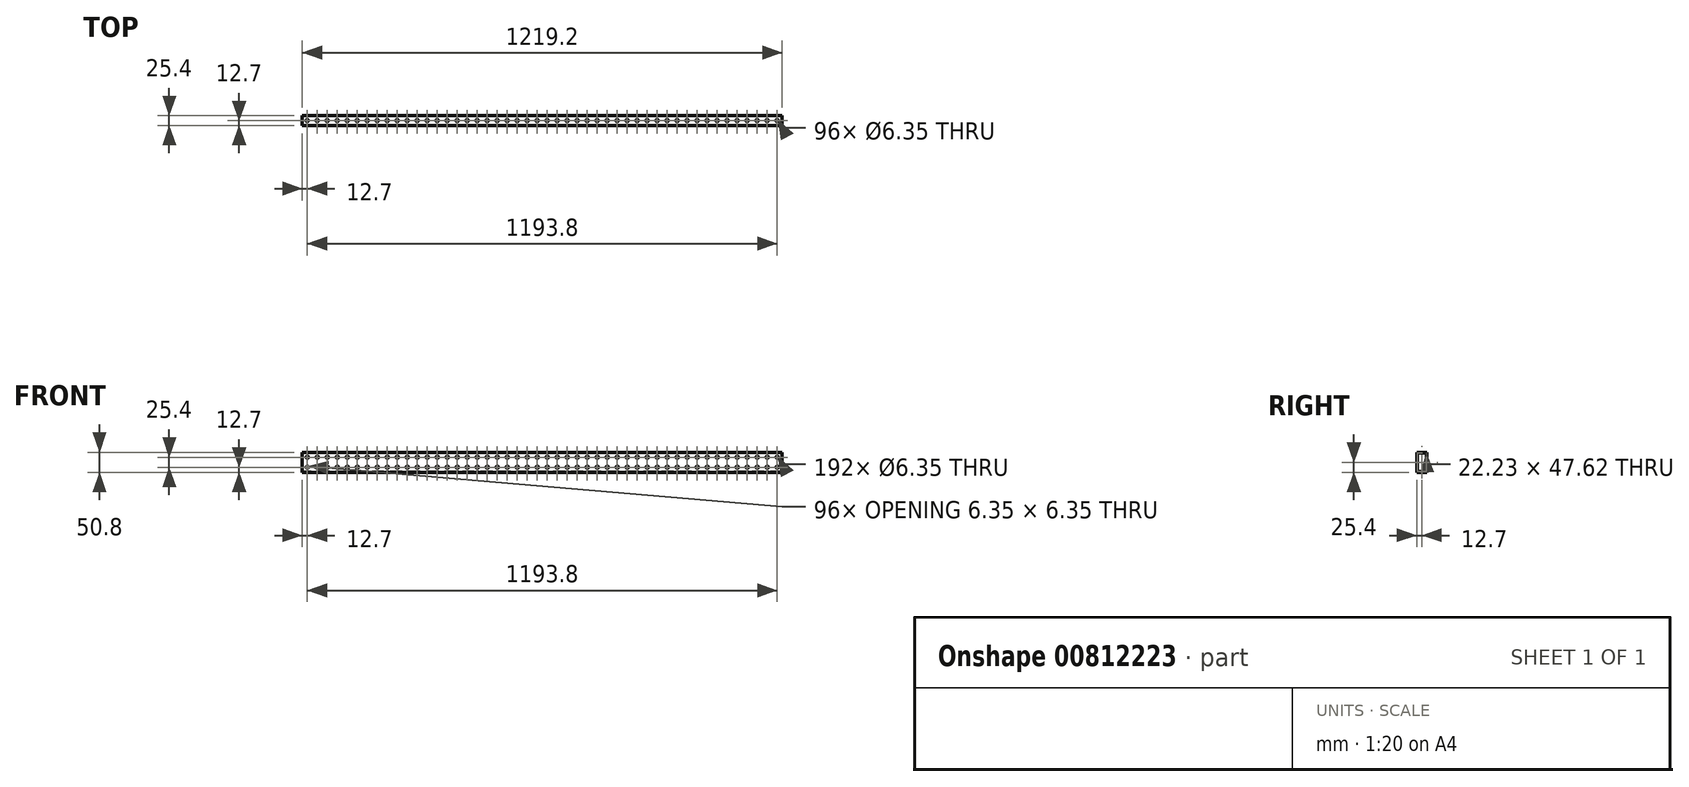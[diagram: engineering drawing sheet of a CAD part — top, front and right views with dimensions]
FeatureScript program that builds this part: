
annotation { "Feature Type Name" : "Feature", "Feature Type Description" : "" }
export const myFeature = defineFeature(function(context is Context, id is Id, definition is map)
    precondition{}
    {
        {
            var Q0;
            Q0=qCreatedBy(makeId("Right.planeOp"),FACE);
            var sketch = newSketch(context, id + "F0", { "sketchPlane" : qUnion([Q0])});
            skLineSegment(sketch, "E0.bottom", {"start": v(-12.7, 25.4) * mm, "end": v(12.7, 25.4) * mm});
            skLineSegment(sketch, "E0.top", {"start": v(-12.7, -25.4) * mm, "end": v(12.7, -25.4) * mm});
            skLineSegment(sketch, "E0.left", {"start": v(-12.7, 25.4) * mm, "end": v(-12.7, -25.4) * mm});
            skLineSegment(sketch, "E0.right", {"start": v(12.7, 25.4) * mm, "end": v(12.7, -25.4) * mm});
            skPoint(sketch, "E0.middle", {"position": v(0, 0) * mm});
            skLineSegment(sketch, "E1.0", {"start": v(-11.11, -23.81) * mm, "end": v(11.11, -23.81) * mm});
            skLineSegment(sketch, "E1.1", {"start": v(-11.11, 23.81) * mm, "end": v(-11.11, -23.81) * mm});
            skLineSegment(sketch, "E1.2", {"start": v(-11.11, 23.81) * mm, "end": v(11.11, 23.81) * mm});
            skLineSegment(sketch, "E1.3", {"start": v(11.11, 23.81) * mm, "end": v(11.11, -23.81) * mm});
            skSolve(sketch);
        }
        {
            var Q0;
            Q0=makeQuery(id+"F0.imprint","IMPRINT",FACE,{"disambiguationData":[TD([[makeQuery(id+"F0.imprint","IMPRINT",EDGE,{"derivedFrom":sQuery(id+"F0.wireOp",EDGE,"E0.bottom")}),-1.0]])]});
            extrude(context, id + "F1", {"entities" : qUnion([Q0]), "depth" : 1219.2 * mm, "offsetDistance" : 25.4 * mm});
        }
        {
            var Q0;
            Q0=makeQuery(id+"F1.opExtrude","SWEPT_FACE",FACE,{"disambiguationData":[OSD([sQuery(id+"F0.wireOp",EDGE,"E0.bottom")])]});
            var sketch = newSketch(context, id + "F2", { "sketchPlane" : qUnion([Q0])});
            skCircle(sketch, "E2", {"center": v(12.7, 0) * mm, "radius": 3.18 * mm});
            skCircle(sketch, "E3.1.0.0", {"center": v(38.1, 0) * mm, "radius": 3.18 * mm});
            skCircle(sketch, "E3.2.0.0", {"center": v(63.5, 0) * mm, "radius": 3.18 * mm});
            skCircle(sketch, "E3.3.0.0", {"center": v(88.9, 0) * mm, "radius": 3.18 * mm});
            skCircle(sketch, "E3.4.0.0", {"center": v(114.3, 0) * mm, "radius": 3.18 * mm});
            skCircle(sketch, "E3.5.0.0", {"center": v(139.7, 0) * mm, "radius": 3.18 * mm});
            skCircle(sketch, "E3.6.0.0", {"center": v(165.1, 0) * mm, "radius": 3.18 * mm});
            skCircle(sketch, "E3.7.0.0", {"center": v(190.5, 0) * mm, "radius": 3.18 * mm});
            skCircle(sketch, "E3.8.0.0", {"center": v(215.9, 0) * mm, "radius": 3.18 * mm});
            skCircle(sketch, "E3.9.0.0", {"center": v(241.3, 0) * mm, "radius": 3.18 * mm});
            skCircle(sketch, "E3.10.0.0", {"center": v(266.7, 0) * mm, "radius": 3.18 * mm});
            skCircle(sketch, "E3.11.0.0", {"center": v(292.1, 0) * mm, "radius": 3.18 * mm});
            skCircle(sketch, "E3.12.0.0", {"center": v(317.5, 0) * mm, "radius": 3.18 * mm});
            skCircle(sketch, "E3.13.0.0", {"center": v(342.9, 0) * mm, "radius": 3.18 * mm});
            skCircle(sketch, "E3.14.0.0", {"center": v(368.3, 0) * mm, "radius": 3.18 * mm});
            skCircle(sketch, "E3.15.0.0", {"center": v(393.7, 0) * mm, "radius": 3.18 * mm});
            skCircle(sketch, "E3.16.0.0", {"center": v(419.1, 0) * mm, "radius": 3.18 * mm});
            skCircle(sketch, "E3.17.0.0", {"center": v(444.5, 0) * mm, "radius": 3.18 * mm});
            skCircle(sketch, "E3.18.0.0", {"center": v(469.9, 0) * mm, "radius": 3.18 * mm});
            skCircle(sketch, "E3.19.0.0", {"center": v(495.3, 0) * mm, "radius": 3.18 * mm});
            skCircle(sketch, "E3.20.0.0", {"center": v(520.7, 0) * mm, "radius": 3.18 * mm});
            skCircle(sketch, "E3.21.0.0", {"center": v(546.1, 0) * mm, "radius": 3.18 * mm});
            skCircle(sketch, "E3.22.0.0", {"center": v(571.5, 0) * mm, "radius": 3.18 * mm});
            skCircle(sketch, "E3.23.0.0", {"center": v(596.9, 0) * mm, "radius": 3.18 * mm});
            skCircle(sketch, "E3.24.0.0", {"center": v(622.3, 0) * mm, "radius": 3.18 * mm});
            skCircle(sketch, "E3.25.0.0", {"center": v(647.7, 0) * mm, "radius": 3.18 * mm});
            skCircle(sketch, "E3.26.0.0", {"center": v(673.1, 0) * mm, "radius": 3.18 * mm});
            skCircle(sketch, "E3.27.0.0", {"center": v(698.5, 0) * mm, "radius": 3.18 * mm});
            skCircle(sketch, "E3.28.0.0", {"center": v(723.9, 0) * mm, "radius": 3.18 * mm});
            skCircle(sketch, "E3.29.0.0", {"center": v(749.3, 0) * mm, "radius": 3.18 * mm});
            skCircle(sketch, "E3.30.0.0", {"center": v(774.7, 0) * mm, "radius": 3.18 * mm});
            skCircle(sketch, "E3.31.0.0", {"center": v(800.1, 0) * mm, "radius": 3.18 * mm});
            skCircle(sketch, "E3.32.0.0", {"center": v(825.5, 0) * mm, "radius": 3.18 * mm});
            skCircle(sketch, "E3.33.0.0", {"center": v(850.9, 0) * mm, "radius": 3.18 * mm});
            skCircle(sketch, "E3.34.0.0", {"center": v(876.3, 0) * mm, "radius": 3.18 * mm});
            skCircle(sketch, "E3.35.0.0", {"center": v(901.7, 0) * mm, "radius": 3.18 * mm});
            skCircle(sketch, "E3.36.0.0", {"center": v(927.1, 0) * mm, "radius": 3.18 * mm});
            skCircle(sketch, "E3.37.0.0", {"center": v(952.5, 0) * mm, "radius": 3.18 * mm});
            skCircle(sketch, "E3.38.0.0", {"center": v(977.9, 0) * mm, "radius": 3.18 * mm});
            skCircle(sketch, "E3.39.0.0", {"center": v(1003.3, 0) * mm, "radius": 3.18 * mm});
            skCircle(sketch, "E3.40.0.0", {"center": v(1028.7, 0) * mm, "radius": 3.18 * mm});
            skCircle(sketch, "E3.41.0.0", {"center": v(1054.1, 0) * mm, "radius": 3.18 * mm});
            skCircle(sketch, "E3.42.0.0", {"center": v(1079.5, 0) * mm, "radius": 3.18 * mm});
            skCircle(sketch, "E3.43.0.0", {"center": v(1104.9, 0) * mm, "radius": 3.18 * mm});
            skCircle(sketch, "E3.44.0.0", {"center": v(1130.3, 0) * mm, "radius": 3.18 * mm});
            skCircle(sketch, "E3.45.0.0", {"center": v(1155.7, 0) * mm, "radius": 3.18 * mm});
            skCircle(sketch, "E3.46.0.0", {"center": v(1181.1, 0) * mm, "radius": 3.18 * mm});
            skCircle(sketch, "E3.47.0.0", {"center": v(1206.5, 0) * mm, "radius": 3.18 * mm});
            skCircle(sketch, "E3.48.0.0", {"center": v(1231.9, 0) * mm, "radius": 3.18 * mm});
            skCircle(sketch, "E3.49.0.0", {"center": v(1257.3, 0) * mm, "radius": 3.18 * mm});
            skCircle(sketch, "E3.50.0.0", {"center": v(1282.7, 0) * mm, "radius": 3.18 * mm});
            skCircle(sketch, "E3.51.0.0", {"center": v(1308.1, 0) * mm, "radius": 3.18 * mm});
            skLineSegment(sketch, "E3.direction1", {"start": v(12.7, 0) * mm, "end": v(38.1, 0) * mm, "construction": true});
            skSolve(sketch);
        }
        {
            var Q0;
            Q0 = qSketchRegion(id + "F2", true);
            extrude(context, id + "F3", {"entities" : qUnion([Q0]), "operationType" : NewBodyOperationType.REMOVE, "endBound" : BoundingType.THROUGH_ALL, "oppositeDirection" : true, "depth" : 25.4 * mm, "offsetDistance" : 25.4 * mm});
        }
        {
            var Q0;
            Q0=makeQuery(id+"F1.opExtrude","SWEPT_FACE",FACE,{"disambiguationData":[OSD([sQuery(id+"F0.wireOp",EDGE,"E0.left")])]});
            var sketch = newSketch(context, id + "F4", { "sketchPlane" : qUnion([Q0])});
            skCircle(sketch, "E4", {"center": v(12.7, 12.7) * mm, "radius": 3.18 * mm});
            skCircle(sketch, "E5.0.1.0", {"center": v(12.7, -12.7) * mm, "radius": 3.18 * mm});
            skCircle(sketch, "E5.1.0.0", {"center": v(38.1, 12.7) * mm, "radius": 3.18 * mm});
            skCircle(sketch, "E5.1.1.0", {"center": v(38.1, -12.7) * mm, "radius": 3.18 * mm});
            skCircle(sketch, "E5.2.0.0", {"center": v(63.5, 12.7) * mm, "radius": 3.18 * mm});
            skCircle(sketch, "E5.2.1.0", {"center": v(63.5, -12.7) * mm, "radius": 3.18 * mm});
            skCircle(sketch, "E5.3.0.0", {"center": v(88.9, 12.7) * mm, "radius": 3.18 * mm});
            skCircle(sketch, "E5.3.1.0", {"center": v(88.9, -12.7) * mm, "radius": 3.18 * mm});
            skCircle(sketch, "E5.4.0.0", {"center": v(114.3, 12.7) * mm, "radius": 3.18 * mm});
            skCircle(sketch, "E5.4.1.0", {"center": v(114.3, -12.7) * mm, "radius": 3.18 * mm});
            skCircle(sketch, "E5.5.0.0", {"center": v(139.7, 12.7) * mm, "radius": 3.18 * mm});
            skCircle(sketch, "E5.5.1.0", {"center": v(139.7, -12.7) * mm, "radius": 3.18 * mm});
            skCircle(sketch, "E5.6.0.0", {"center": v(165.1, 12.7) * mm, "radius": 3.18 * mm});
            skCircle(sketch, "E5.6.1.0", {"center": v(165.1, -12.7) * mm, "radius": 3.18 * mm});
            skCircle(sketch, "E5.7.0.0", {"center": v(190.5, 12.7) * mm, "radius": 3.18 * mm});
            skCircle(sketch, "E5.7.1.0", {"center": v(190.5, -12.7) * mm, "radius": 3.18 * mm});
            skCircle(sketch, "E5.8.0.0", {"center": v(215.9, 12.7) * mm, "radius": 3.18 * mm});
            skCircle(sketch, "E5.8.1.0", {"center": v(215.9, -12.7) * mm, "radius": 3.18 * mm});
            skCircle(sketch, "E5.9.0.0", {"center": v(241.3, 12.7) * mm, "radius": 3.18 * mm});
            skCircle(sketch, "E5.9.1.0", {"center": v(241.3, -12.7) * mm, "radius": 3.18 * mm});
            skCircle(sketch, "E5.10.0.0", {"center": v(266.7, 12.7) * mm, "radius": 3.18 * mm});
            skCircle(sketch, "E5.10.1.0", {"center": v(266.7, -12.7) * mm, "radius": 3.18 * mm});
            skCircle(sketch, "E5.11.0.0", {"center": v(292.1, 12.7) * mm, "radius": 3.18 * mm});
            skCircle(sketch, "E5.11.1.0", {"center": v(292.1, -12.7) * mm, "radius": 3.18 * mm});
            skCircle(sketch, "E5.12.0.0", {"center": v(317.5, 12.7) * mm, "radius": 3.18 * mm});
            skCircle(sketch, "E5.12.1.0", {"center": v(317.5, -12.7) * mm, "radius": 3.18 * mm});
            skCircle(sketch, "E5.13.0.0", {"center": v(342.9, 12.7) * mm, "radius": 3.18 * mm});
            skCircle(sketch, "E5.13.1.0", {"center": v(342.9, -12.7) * mm, "radius": 3.18 * mm});
            skCircle(sketch, "E5.14.0.0", {"center": v(368.3, 12.7) * mm, "radius": 3.18 * mm});
            skCircle(sketch, "E5.14.1.0", {"center": v(368.3, -12.7) * mm, "radius": 3.18 * mm});
            skCircle(sketch, "E5.15.0.0", {"center": v(393.7, 12.7) * mm, "radius": 3.18 * mm});
            skCircle(sketch, "E5.15.1.0", {"center": v(393.7, -12.7) * mm, "radius": 3.18 * mm});
            skCircle(sketch, "E5.16.0.0", {"center": v(419.1, 12.7) * mm, "radius": 3.18 * mm});
            skCircle(sketch, "E5.16.1.0", {"center": v(419.1, -12.7) * mm, "radius": 3.18 * mm});
            skCircle(sketch, "E5.17.0.0", {"center": v(444.5, 12.7) * mm, "radius": 3.18 * mm});
            skCircle(sketch, "E5.17.1.0", {"center": v(444.5, -12.7) * mm, "radius": 3.18 * mm});
            skCircle(sketch, "E5.18.0.0", {"center": v(469.9, 12.7) * mm, "radius": 3.18 * mm});
            skCircle(sketch, "E5.18.1.0", {"center": v(469.9, -12.7) * mm, "radius": 3.18 * mm});
            skCircle(sketch, "E5.19.0.0", {"center": v(495.3, 12.7) * mm, "radius": 3.18 * mm});
            skCircle(sketch, "E5.19.1.0", {"center": v(495.3, -12.7) * mm, "radius": 3.18 * mm});
            skCircle(sketch, "E5.20.0.0", {"center": v(520.7, 12.7) * mm, "radius": 3.18 * mm});
            skCircle(sketch, "E5.20.1.0", {"center": v(520.7, -12.7) * mm, "radius": 3.18 * mm});
            skCircle(sketch, "E5.21.0.0", {"center": v(546.1, 12.7) * mm, "radius": 3.18 * mm});
            skCircle(sketch, "E5.21.1.0", {"center": v(546.1, -12.7) * mm, "radius": 3.18 * mm});
            skCircle(sketch, "E5.22.0.0", {"center": v(571.5, 12.7) * mm, "radius": 3.18 * mm});
            skCircle(sketch, "E5.22.1.0", {"center": v(571.5, -12.7) * mm, "radius": 3.18 * mm});
            skCircle(sketch, "E5.23.0.0", {"center": v(596.9, 12.7) * mm, "radius": 3.18 * mm});
            skCircle(sketch, "E5.23.1.0", {"center": v(596.9, -12.7) * mm, "radius": 3.18 * mm});
            skCircle(sketch, "E5.24.0.0", {"center": v(622.3, 12.7) * mm, "radius": 3.18 * mm});
            skCircle(sketch, "E5.24.1.0", {"center": v(622.3, -12.7) * mm, "radius": 3.18 * mm});
            skCircle(sketch, "E5.25.0.0", {"center": v(647.7, 12.7) * mm, "radius": 3.18 * mm});
            skCircle(sketch, "E5.25.1.0", {"center": v(647.7, -12.7) * mm, "radius": 3.18 * mm});
            skCircle(sketch, "E5.26.0.0", {"center": v(673.1, 12.7) * mm, "radius": 3.18 * mm});
            skCircle(sketch, "E5.26.1.0", {"center": v(673.1, -12.7) * mm, "radius": 3.18 * mm});
            skCircle(sketch, "E5.27.0.0", {"center": v(698.5, 12.7) * mm, "radius": 3.18 * mm});
            skCircle(sketch, "E5.27.1.0", {"center": v(698.5, -12.7) * mm, "radius": 3.18 * mm});
            skCircle(sketch, "E5.28.0.0", {"center": v(723.9, 12.7) * mm, "radius": 3.18 * mm});
            skCircle(sketch, "E5.28.1.0", {"center": v(723.9, -12.7) * mm, "radius": 3.18 * mm});
            skCircle(sketch, "E5.29.0.0", {"center": v(749.3, 12.7) * mm, "radius": 3.18 * mm});
            skCircle(sketch, "E5.29.1.0", {"center": v(749.3, -12.7) * mm, "radius": 3.18 * mm});
            skCircle(sketch, "E5.30.0.0", {"center": v(774.7, 12.7) * mm, "radius": 3.18 * mm});
            skCircle(sketch, "E5.30.1.0", {"center": v(774.7, -12.7) * mm, "radius": 3.18 * mm});
            skCircle(sketch, "E5.31.0.0", {"center": v(800.1, 12.7) * mm, "radius": 3.18 * mm});
            skCircle(sketch, "E5.31.1.0", {"center": v(800.1, -12.7) * mm, "radius": 3.18 * mm});
            skCircle(sketch, "E5.32.0.0", {"center": v(825.5, 12.7) * mm, "radius": 3.18 * mm});
            skCircle(sketch, "E5.32.1.0", {"center": v(825.5, -12.7) * mm, "radius": 3.18 * mm});
            skCircle(sketch, "E5.33.0.0", {"center": v(850.9, 12.7) * mm, "radius": 3.18 * mm});
            skCircle(sketch, "E5.33.1.0", {"center": v(850.9, -12.7) * mm, "radius": 3.18 * mm});
            skCircle(sketch, "E5.34.0.0", {"center": v(876.3, 12.7) * mm, "radius": 3.18 * mm});
            skCircle(sketch, "E5.34.1.0", {"center": v(876.3, -12.7) * mm, "radius": 3.18 * mm});
            skCircle(sketch, "E5.35.0.0", {"center": v(901.7, 12.7) * mm, "radius": 3.18 * mm});
            skCircle(sketch, "E5.35.1.0", {"center": v(901.7, -12.7) * mm, "radius": 3.18 * mm});
            skCircle(sketch, "E5.36.0.0", {"center": v(927.1, 12.7) * mm, "radius": 3.18 * mm});
            skCircle(sketch, "E5.36.1.0", {"center": v(927.1, -12.7) * mm, "radius": 3.18 * mm});
            skCircle(sketch, "E5.37.0.0", {"center": v(952.5, 12.7) * mm, "radius": 3.18 * mm});
            skCircle(sketch, "E5.37.1.0", {"center": v(952.5, -12.7) * mm, "radius": 3.18 * mm});
            skCircle(sketch, "E5.38.0.0", {"center": v(977.9, 12.7) * mm, "radius": 3.18 * mm});
            skCircle(sketch, "E5.38.1.0", {"center": v(977.9, -12.7) * mm, "radius": 3.18 * mm});
            skCircle(sketch, "E5.39.0.0", {"center": v(1003.3, 12.7) * mm, "radius": 3.18 * mm});
            skCircle(sketch, "E5.39.1.0", {"center": v(1003.3, -12.7) * mm, "radius": 3.18 * mm});
            skCircle(sketch, "E5.40.0.0", {"center": v(1028.7, 12.7) * mm, "radius": 3.18 * mm});
            skCircle(sketch, "E5.40.1.0", {"center": v(1028.7, -12.7) * mm, "radius": 3.18 * mm});
            skCircle(sketch, "E5.41.0.0", {"center": v(1054.1, 12.7) * mm, "radius": 3.18 * mm});
            skCircle(sketch, "E5.41.1.0", {"center": v(1054.1, -12.7) * mm, "radius": 3.18 * mm});
            skCircle(sketch, "E5.42.0.0", {"center": v(1079.5, 12.7) * mm, "radius": 3.18 * mm});
            skCircle(sketch, "E5.42.1.0", {"center": v(1079.5, -12.7) * mm, "radius": 3.18 * mm});
            skCircle(sketch, "E5.43.0.0", {"center": v(1104.9, 12.7) * mm, "radius": 3.18 * mm});
            skCircle(sketch, "E5.43.1.0", {"center": v(1104.9, -12.7) * mm, "radius": 3.18 * mm});
            skCircle(sketch, "E5.44.0.0", {"center": v(1130.3, 12.7) * mm, "radius": 3.18 * mm});
            skCircle(sketch, "E5.44.1.0", {"center": v(1130.3, -12.7) * mm, "radius": 3.18 * mm});
            skCircle(sketch, "E5.45.0.0", {"center": v(1155.7, 12.7) * mm, "radius": 3.18 * mm});
            skCircle(sketch, "E5.45.1.0", {"center": v(1155.7, -12.7) * mm, "radius": 3.18 * mm});
            skCircle(sketch, "E5.46.0.0", {"center": v(1181.1, 12.7) * mm, "radius": 3.18 * mm});
            skCircle(sketch, "E5.46.1.0", {"center": v(1181.1, -12.7) * mm, "radius": 3.18 * mm});
            skCircle(sketch, "E5.47.0.0", {"center": v(1206.5, 12.7) * mm, "radius": 3.18 * mm});
            skCircle(sketch, "E5.47.1.0", {"center": v(1206.5, -12.7) * mm, "radius": 3.18 * mm});
            skCircle(sketch, "E5.48.0.0", {"center": v(1231.9, 12.7) * mm, "radius": 3.18 * mm});
            skCircle(sketch, "E5.48.1.0", {"center": v(1231.9, -12.7) * mm, "radius": 3.18 * mm});
            skCircle(sketch, "E5.49.0.0", {"center": v(1257.3, 12.7) * mm, "radius": 3.18 * mm});
            skCircle(sketch, "E5.49.1.0", {"center": v(1257.3, -12.7) * mm, "radius": 3.18 * mm});
            skCircle(sketch, "E5.50.0.0", {"center": v(1282.7, 12.7) * mm, "radius": 3.18 * mm});
            skCircle(sketch, "E5.50.1.0", {"center": v(1282.7, -12.7) * mm, "radius": 3.18 * mm});
            skCircle(sketch, "E5.51.0.0", {"center": v(1308.1, 12.7) * mm, "radius": 3.18 * mm});
            skCircle(sketch, "E5.51.1.0", {"center": v(1308.1, -12.7) * mm, "radius": 3.18 * mm});
            skLineSegment(sketch, "E5.direction1", {"start": v(12.7, 12.7) * mm, "end": v(38.1, 12.7) * mm, "construction": true});
            skLineSegment(sketch, "E5.direction2", {"start": v(12.7, 12.7) * mm, "end": v(12.7, -12.7) * mm, "construction": true});
            skSolve(sketch);
        }
        {
            var Q0;
            Q0 = qSketchRegion(id + "F4", true);
            extrude(context, id + "F5", {"entities" : qUnion([Q0]), "operationType" : NewBodyOperationType.REMOVE, "oppositeDirection" : true, "depth" : 25.4 * mm, "offsetDistance" : 25.4 * mm});
        }
    });
